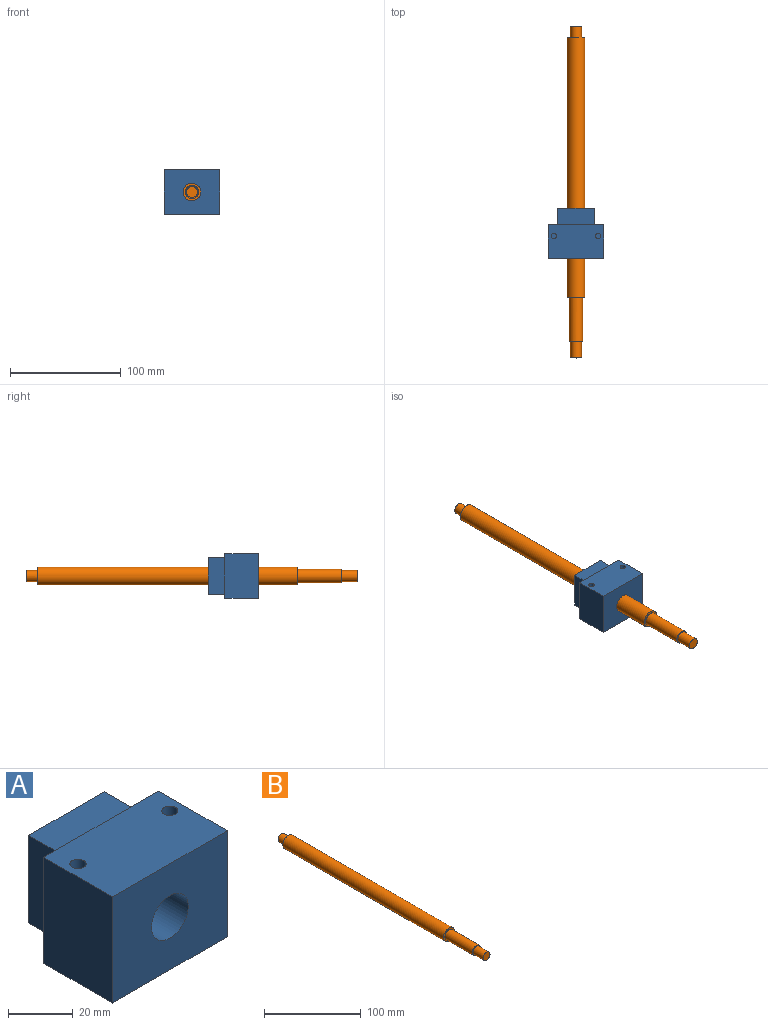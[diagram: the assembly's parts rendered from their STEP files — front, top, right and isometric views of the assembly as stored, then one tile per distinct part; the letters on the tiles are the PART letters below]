
ASSEMBLY  parts=2 mates=1
PART A: 16 faces, bbox 50x45x40 mm
  f0: plane 50x30mm, normal (0,0,1), area 1460.7mm2, adj f2,f3,f4,f5,f12,f14
  f1: plane 50x30mm, normal (0,0,-1), area 1500mm2, adj f2,f3,f4,f5
  f2: plane 40x30mm, normal (1,0,0), area 1200mm2, adj f0,f1,f4,f5
  f3: plane 40x30mm, normal (-1,0,0), area 1200mm2, adj f0,f1,f4,f5
  f4: plane 50x40mm, normal (0,1,0), area 911mm2, adj f0,f1,f2,f3,f6,f7,f8,f9
  f5: plane 50x40mm, normal (0,-1,0), area 1798.9mm2, adj f0,f1,f2,f3,f10
  f6: plane 33x15mm, normal (1,0,0), area 495mm2, adj f4,f7,f9,f11
  f7: plane 33x15mm, normal (0,0,-1), area 495mm2, adj f4,f6,f8,f11
  f8: plane 33x15mm, normal (-1,0,0), area 495mm2, adj f4,f7,f9,f11
  f9: plane 33x15mm, normal (0,0,1), area 495mm2, adj f4,f6,f8,f11
  f10: cylinder r=8mm len=45mm, axis (0,-1,0), area 2261.9mm2, adj f5,f11
  f11: plane 33x33mm, normal (0,1,0), area 887.9mm2, adj f6,f7,f8,f9,f10
  f12: cylinder r=2.5mm len=5mm, axis (0,0,1), area 78.5mm2, adj f0,f13
  f13: plane 5x5mm, normal (0,0,1), area 19.6mm2, adj f12
  f14: cylinder r=2.5mm len=5mm, axis (0,0,1), area 78.5mm2, adj f0,f15
  f15: plane 5x5mm, normal (0,0,1), area 19.6mm2, adj f14
PART B: 9 faces, bbox 16x300x16 mm
  f0: cylinder r=8mm len=235mm, axis (0,-1,0), area 11812.4mm2, adj f1,f2
  f1: plane 16x16mm, normal (0,1,0), area 122.5mm2, adj f0,f7
  f2: plane 16x16mm, normal (0,-1,0), area 88mm2, adj f0,f3
  f3: cylinder r=6mm len=40mm, axis (0,-1,0), area 1508mm2, adj f2,f4
  f4: plane 12x12mm, normal (0,-1,0), area 34.6mm2, adj f3,f5
  f5: cylinder r=5mm len=15mm, axis (0,-1,0), area 471.2mm2, adj f4,f6
  f6: plane 10x10mm, normal (0,-1,0), area 78.5mm2, adj f5
  f7: cylinder r=5mm len=10mm, axis (0,-1,0), area 314.2mm2, adj f1,f8
  f8: plane 10x10mm, normal (0,1,0), area 78.5mm2, adj f7
PLACE A t=(-33.67,35.22,11.08)mm
PLACE B t=(-33.67,0,11.08)mm fixed
MATE slider B.f0 <-> A.f10  axis (0,-1,0) through (-33.67,0,11.08)mm
